# Revit family: VTC-CeilingMount
name_source: partatom
category: Lighting Fixtures
units: mm (PartAtom-declared; Revit-internal decimal feet)

## family parameters
Cut with Voids When Loaded = No
Host = Face
Light Source = Yes
OmniClass Number = 23.80.70.11
OmniClass Title = Luminaries for Internal Lighting
Part Type = Normal
Room Calculation Point = No
Round Connector Dimension = Use Diameter
Shared = Yes

## types (1)
- VTC
    Apparent Load = 0 VA
    Assembly Code = D5020200
    CCT = 5000K
    Color Filter = 16777215
    Colour = Gray
    Default Elevation = 48"
    Description = LED Vaportite, die cast housing, glass globe
    Dimming Lamp Color Temperature Shift = <None>
    Distribution = Type II
    Emit Shape Visible in Rendering = No
    Emit from Circle Diameter = 5 1/2"
    Glass = Glass  White
    Lamp = 1
    Load Classification = Lighting
    Manufacturer = Columbia Lighting
    Model = VTC
    Photometric Notes = More IES files download in Photometrics Web Link
    Photometric Web File = VTC-5K-G-U-P2-G-GR.ies
    Pole Height = 120"
    Power Factor = 1
    Tilt Angle = 90.00°
    Type Comments = Lighting Fixture
    URL = https://www.currentlighting.com
    Voltage = 120 V
    Warranty = Five year limited warranty
    Wattage Comments = 27W

## geometry (parser evidence)
native form markers: Sweep x4
no freeform markers — native parametric forms only
